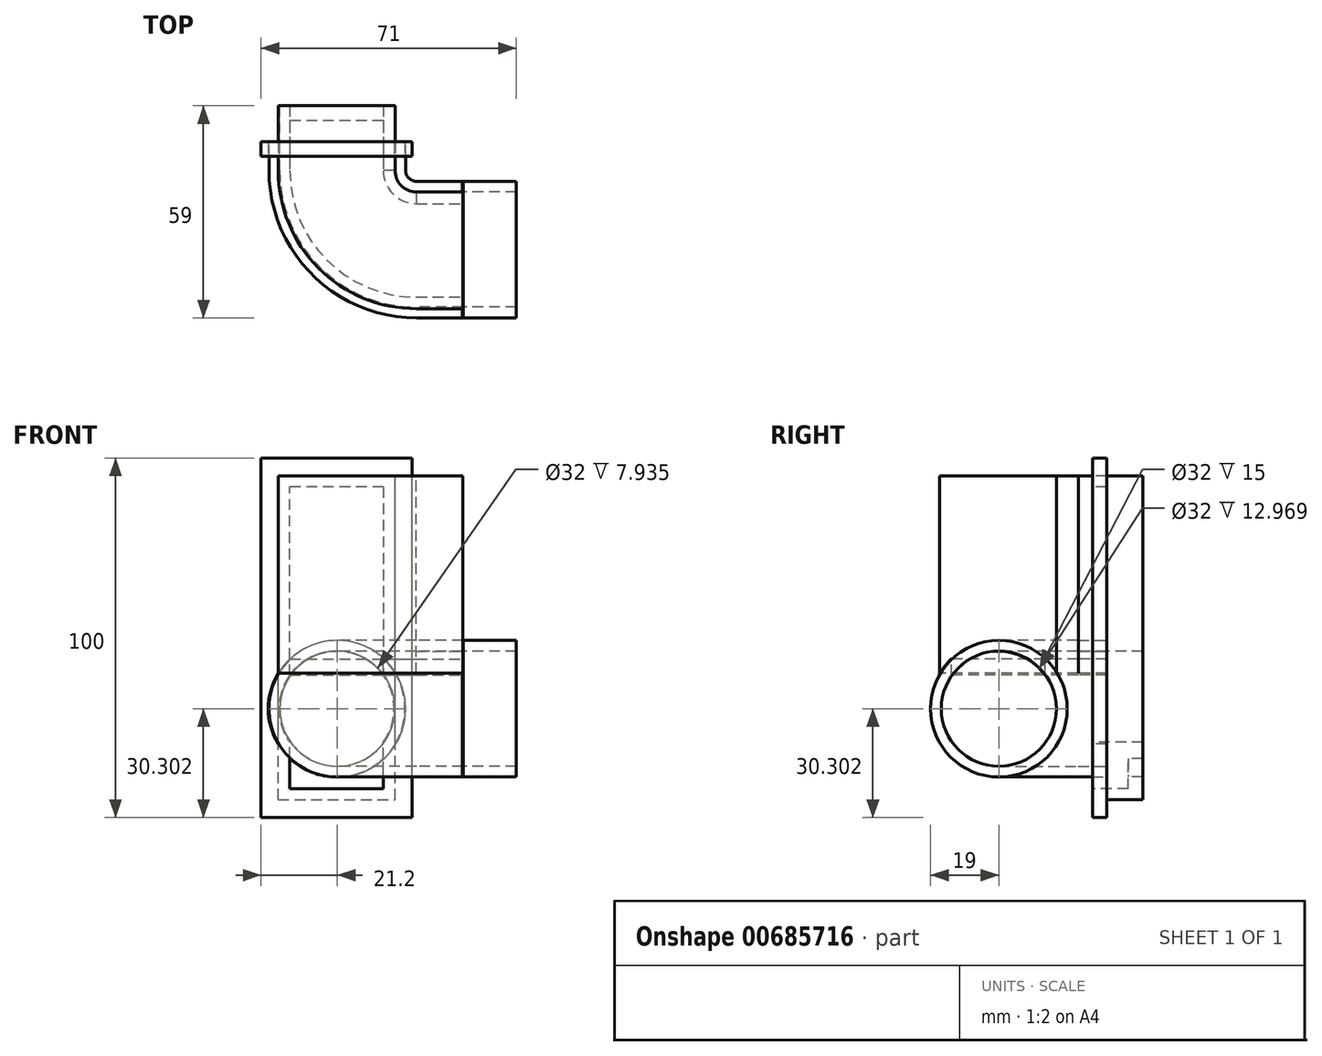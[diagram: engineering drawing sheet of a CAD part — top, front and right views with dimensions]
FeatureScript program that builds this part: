
annotation { "Feature Type Name" : "Feature", "Feature Type Description" : "" }
export const myFeature = defineFeature(function(context is Context, id is Id, definition is map)
    precondition{}
    {
        {
            var Q0;
            Q0=qCreatedBy(makeId("Front.planeOp"),FACE);
            var sketch = newSketch(context, id + "F0", { "sketchPlane" : qUnion([Q0])});
            skLineSegment(sketch, "E0.bottom", {"start": v(-16.25, -45) * mm, "end": v(16.25, -45) * mm});
            skLineSegment(sketch, "E0.top", {"start": v(-16.25, 45) * mm, "end": v(16.25, 45) * mm});
            skLineSegment(sketch, "E0.left", {"start": v(-16.25, -45) * mm, "end": v(-16.25, 45) * mm});
            skLineSegment(sketch, "E0.right", {"start": v(16.25, -45) * mm, "end": v(16.25, 45) * mm});
            skPoint(sketch, "E0.middle", {"position": v(0, 0) * mm});
            skLineSegment(sketch, "E1.bottom", {"start": v(-13, -42) * mm, "end": v(13, -42) * mm});
            skLineSegment(sketch, "E1.top", {"start": v(-13, 42) * mm, "end": v(13, 42) * mm});
            skLineSegment(sketch, "E1.left", {"start": v(-13, -42) * mm, "end": v(-13, 42) * mm});
            skLineSegment(sketch, "E1.right", {"start": v(13, -42) * mm, "end": v(13, 42) * mm});
            skLineSegment(sketch, "E2.bottom", {"start": v(-21, -50) * mm, "end": v(21, -50) * mm});
            skLineSegment(sketch, "E2.top", {"start": v(-21, 50) * mm, "end": v(21, 50) * mm});
            skLineSegment(sketch, "E2.left", {"start": v(-21, -50) * mm, "end": v(-21, 50) * mm});
            skLineSegment(sketch, "E2.right", {"start": v(21, -50) * mm, "end": v(21, 50) * mm});
            skCircle(sketch, "E3", {"center": v(0, -19.7) * mm, "radius": 19 * mm});
            skCircle(sketch, "E4", {"center": v(0, -19.7) * mm, "radius": 16 * mm});
            skSolve(sketch);
        }
        {
            var Q0;
            Q0=makeQuery(id+"F0.imprint","IMPRINT",FACE,{"disambiguationData":[TD([[makeQuery(id+"F0.imprint","IMPRINT",EDGE,{"derivedFrom":sQuery(id+"F0.wireOp",EDGE,"E0.bottom")}),1.0]])]});
            var Q1;
            {var subQ1=sQuery(id+"F0.wireOp",EDGE,"E0.top");Q1=makeQuery(id+"F0.imprint","IMPRINT",FACE,{"disambiguationData":[TD([[makeQuery(id+"F0.imprint","IMPRINT",EDGE,{"derivedFrom":subQ1}),-1.0]])]});}
            var Q2;
            {var subQ0=sQuery(id+"F0.wireOp",EDGE,"E4");var subQ1=sQuery(id+"F0.wireOp",EDGE,"E0.left");var subQ2=makeQuery(id+"F0.imprint","INTERSECT",VERTEX,{"derivedFrom":[subQ1,subQ0]});Q2=makeQuery(id+"F0.imprint","IMPRINT",FACE,{"disambiguationData":[TD([[makeQuery(id+"F0.imprint","IMPRINT",EDGE,{"disambiguationData":[TD([[subQ2,-1.0]])],"derivedFrom":subQ1}),-1.0]])]});}
            var Q3;
            {var subQ0=sQuery(id+"F0.wireOp",EDGE,"E3");var subQ1=sQuery(id+"F0.wireOp",EDGE,"E0.left");var subQ2=makeQuery(id+"F0.imprint","INTERSECT",VERTEX,{"disambiguationData":[OD(0.0)],"derivedFrom":[subQ1,subQ0]});Q3=makeQuery(id+"F0.imprint","IMPRINT",FACE,{"disambiguationData":[TD([[makeQuery(id+"F0.imprint","IMPRINT",EDGE,{"disambiguationData":[TD([[subQ2,-1.0]])],"derivedFrom":subQ1}),-1.0]])]});}
            var Q4;
            {var subQ0=sQuery(id+"F0.wireOp",EDGE,"E3");var subQ1=sQuery(id+"F0.wireOp",EDGE,"E0.right");var subQ2=makeQuery(id+"F0.imprint","INTERSECT",VERTEX,{"disambiguationData":[OD(0.0)],"derivedFrom":[subQ1,subQ0]});Q4=makeQuery(id+"F0.imprint","IMPRINT",FACE,{"disambiguationData":[TD([[makeQuery(id+"F0.imprint","IMPRINT",EDGE,{"disambiguationData":[TD([[subQ2,-1.0]])],"derivedFrom":subQ1}),1.0]])]});}
            var Q5;
            {var subQ0=sQuery(id+"F0.wireOp",EDGE,"E4");var subQ1=sQuery(id+"F0.wireOp",EDGE,"E0.right");var subQ2=makeQuery(id+"F0.imprint","INTERSECT",VERTEX,{"derivedFrom":[subQ1,subQ0]});Q5=makeQuery(id+"F0.imprint","IMPRINT",FACE,{"disambiguationData":[TD([[makeQuery(id+"F0.imprint","IMPRINT",EDGE,{"disambiguationData":[TD([[subQ2,-1.0]])],"derivedFrom":subQ1}),1.0]])]});}
            extrude(context, id + "F1", {"entities" : qUnion([Q0, Q1, Q2, Q3, Q4, Q5]), "oppositeDirection" : true, "depth" : 40 * mm, "offsetDistance" : 25 * mm, "hasSecondDirection" : true, "secondDirectionOppositeDirection" : true, "secondDirectionDepth" : 26 * mm});
        }
        {
            var Q0;
            {var subQ1=sQuery(id+"F0.wireOp",EDGE,"E0.bottom");Q0=makeQuery(id+"F0.imprint","IMPRINT",FACE,{"disambiguationData":[TD([[makeQuery(id+"F0.imprint","IMPRINT",EDGE,{"derivedFrom":subQ1}),-1.0]])]});}
            var Q1;
            {var subQ0=sQuery(id+"F0.wireOp",EDGE,"E3");var subQ1=sQuery(id+"F0.wireOp",EDGE,"E0.right");var subQ2=makeQuery(id+"F0.imprint","INTERSECT",VERTEX,{"disambiguationData":[OD(0.0)],"derivedFrom":[subQ1,subQ0]});Q1=makeQuery(id+"F0.imprint","IMPRINT",FACE,{"disambiguationData":[TD([[makeQuery(id+"F0.imprint","IMPRINT",EDGE,{"disambiguationData":[TD([[subQ2,-1.0]])],"derivedFrom":subQ1}),-1.0]])]});}
            var Q2;
            {var subQ0=sQuery(id+"F0.wireOp",EDGE,"E3");var subQ1=sQuery(id+"F0.wireOp",EDGE,"E0.left");var subQ2=makeQuery(id+"F0.imprint","INTERSECT",VERTEX,{"disambiguationData":[OD(0.0)],"derivedFrom":[subQ1,subQ0]});Q2=makeQuery(id+"F0.imprint","IMPRINT",FACE,{"disambiguationData":[TD([[makeQuery(id+"F0.imprint","IMPRINT",EDGE,{"disambiguationData":[TD([[subQ2,-1.0]])],"derivedFrom":subQ1}),1.0]])]});}
            extrude(context, id + "F2", {"entities" : qUnion([Q0, Q1, Q2]), "operationType" : NewBodyOperationType.ADD, "oppositeDirection" : true, "depth" : 30 * mm, "offsetDistance" : 25 * mm, "hasSecondDirection" : true, "secondDirectionOppositeDirection" : true, "secondDirectionDepth" : 26 * mm});
        }
        {
            var Q0;
            {var subQ0=sQuery(id+"F0.wireOp",EDGE,"E4");var subQ1=sQuery(id+"F0.wireOp",EDGE,"E1.left");var subQ2=makeQuery(id+"F0.imprint","INTERSECT",VERTEX,{"disambiguationData":[OD(1.0)],"derivedFrom":[subQ1,subQ0]});Q0=makeQuery(id+"F0.imprint","IMPRINT",FACE,{"disambiguationData":[TD([[makeQuery(id+"F0.imprint","IMPRINT",EDGE,{"disambiguationData":[TD([[subQ2,-1.0]])],"derivedFrom":subQ1}),-1.0]])]});}
            var Q1;
            {var subQ0=sQuery(id+"F0.wireOp",EDGE,"E3");var subQ1=sQuery(id+"F0.wireOp",EDGE,"E1.left");var subQ2=makeQuery(id+"F0.imprint","INTERSECT",VERTEX,{"disambiguationData":[OD(0.0)],"derivedFrom":[subQ1,subQ0]});Q1=makeQuery(id+"F0.imprint","IMPRINT",FACE,{"disambiguationData":[TD([[makeQuery(id+"F0.imprint","IMPRINT",EDGE,{"disambiguationData":[TD([[subQ2,-1.0]])],"derivedFrom":subQ1}),-1.0]])]});}
            var Q2;
            {var subQ0=sQuery(id+"F0.wireOp",EDGE,"E3");var subQ1=sQuery(id+"F0.wireOp",EDGE,"E0.left");var subQ9=makeQuery(id+"F0.imprint","INTERSECT",VERTEX,{"disambiguationData":[OD(0.0)],"derivedFrom":[subQ1,subQ0]});Q2=makeQuery(id+"F0.imprint","IMPRINT",FACE,{"disambiguationData":[TD([[makeQuery(id+"F0.imprint","IMPRINT",EDGE,{"disambiguationData":[TD([[subQ9,-1.0]])],"derivedFrom":subQ1}),-1.0]])]});}
            var Q3;
            {var subQ0=sQuery(id+"F0.wireOp",EDGE,"E3");var subQ1=sQuery(id+"F0.wireOp",EDGE,"E0.right");var subQ9=makeQuery(id+"F0.imprint","INTERSECT",VERTEX,{"disambiguationData":[OD(0.0)],"derivedFrom":[subQ1,subQ0]});Q3=makeQuery(id+"F0.imprint","IMPRINT",FACE,{"disambiguationData":[TD([[makeQuery(id+"F0.imprint","IMPRINT",EDGE,{"disambiguationData":[TD([[subQ9,-1.0]])],"derivedFrom":subQ1}),1.0]])]});}
            extrude(context, id + "F3", {"entities" : qUnion([Q0, Q1, Q2, Q3]), "oppositeDirection" : true, "depth" : 40 * mm, "offsetDistance" : 25 * mm, "hasSecondDirection" : true, "secondDirectionOppositeDirection" : false, "secondDirectionDepth" : -30 * mm});
        }
        {
            var Q0;
            Q0=qCreatedBy(makeId("Right.planeOp"),FACE);
            var sketch = newSketch(context, id + "F4", { "sketchPlane" : qUnion([Q0])});
            skCircle(sketch, "E5", {"center": v(0, -19.7) * mm, "radius": 19 * mm});
            skCircle(sketch, "E6", {"center": v(0, -19.7) * mm, "radius": 16 * mm});
            skSolve(sketch);
        }
        {
            var Q0;
            Q0=makeQuery(id+"F4.imprint","IMPRINT",FACE,{"disambiguationData":[TD([[makeQuery(id+"F4.imprint","IMPRINT",EDGE,{"derivedFrom":sQuery(id+"F4.wireOp",EDGE,"E5")}),1.0]])]});
            var Q1;
            Q1 = qSketchRegion(id + "F6", true);
            extrude(context, id + "F5", {"entities" : qUnion([Q0, Q1]), "depth" : 50 * mm, "offsetDistance" : 25 * mm, "hasSecondDirection" : true, "secondDirectionOppositeDirection" : false, "secondDirectionDepth" : 35 * mm});
        }
        {
            var Q0;
            Q0=qCreatedBy(makeId("Top.planeOp"),FACE);
            var sketch = newSketch(context, id + "F6", { "sketchPlane" : qUnion([Q0])});
            skLineSegment(sketch, "E7", {"start": v(0.2, 22) * mm, "end": v(0.2, 29.94) * mm});
            skLineSegment(sketch, "E8", {"start": v(22.2, 0) * mm, "end": v(35.17, 0) * mm});
            skArc(sketch, "E9", {"start": v(0.2, 22) * mm, "mid": v(6.64, 6.44) * mm, "end": v(22.2, 0) * mm});
            skLineSegment(sketch, "E10.0", {"start": v(-18.8, 22) * mm, "end": v(-18.8, 29.94) * mm});
            skArc(sketch, "E10.1", {"start": v(-18.8, 22) * mm, "mid": v(-6.8, -7) * mm, "end": v(22.2, -19) * mm});
            skLineSegment(sketch, "E10.2", {"start": v(22.2, -19) * mm, "end": v(35.17, -19) * mm});
            skLineSegment(sketch, "E11.0", {"start": v(19.2, 22) * mm, "end": v(19.2, 29.94) * mm});
            skArc(sketch, "E11.1", {"start": v(19.2, 22) * mm, "mid": v(20.08, 19.88) * mm, "end": v(22.2, 19) * mm});
            skLineSegment(sketch, "E11.2", {"start": v(22.2, 19) * mm, "end": v(35.17, 19) * mm});
            skSolve(sketch);
        }
        {
            var Q0;
            Q0=makeQuery(id+"F3.opExtrude","CAP_FACE",FACE,{"disambiguationData":[OSD([sQuery(id+"F0.wireOp",EDGE,"E3"),sQuery(id+"F0.wireOp",EDGE,"E4")])],"isStart":true});
            var Q1;
            Q1=makeQuery(id+"F5.opExtrude","CAP_FACE",FACE,{"disambiguationData":[OSD([sQuery(id+"F4.wireOp",EDGE,"E5"),sQuery(id+"F4.wireOp",EDGE,"E6")])],"isStart":true});
            var Q2;
            Q2=sQuery(id+"F6.wireOp",EDGE,"E11.0");
            var Q3;
            Q3=sQuery(id+"F6.wireOp",EDGE,"E11.1");
            var Q4;
            Q4=sQuery(id+"F6.wireOp",EDGE,"E11.2");
            sweep(context, id + "F7", {"profiles" : qUnion([Q0, Q1]), "path" : qUnion([Q2, Q3, Q4])});
        }
        {
            var Q0;
            {var subQ0=sQuery(id+"F0.wireOp",EDGE,"E1.top");Q0=makeQuery(id+"F0.imprint","IMPRINT",FACE,{"disambiguationData":[TD([[makeQuery(id+"F0.imprint","IMPRINT",EDGE,{"derivedFrom":subQ0}),-1.0]])]});}
            var Q1;
            {var subQ0=sQuery(id+"F0.wireOp",EDGE,"E1.bottom");Q1=makeQuery(id+"F0.imprint","IMPRINT",FACE,{"disambiguationData":[TD([[makeQuery(id+"F0.imprint","IMPRINT",EDGE,{"derivedFrom":subQ0}),1.0]])]});}
            extrude(context, id + "F8", {"entities" : qUnion([Q0, Q1]), "operationType" : NewBodyOperationType.ADD, "oppositeDirection" : true, "depth" : 40 * mm, "offsetDistance" : 25 * mm, "hasSecondDirection" : true, "secondDirectionOppositeDirection" : true, "secondDirectionDepth" : 36 * mm});
        }
    });
